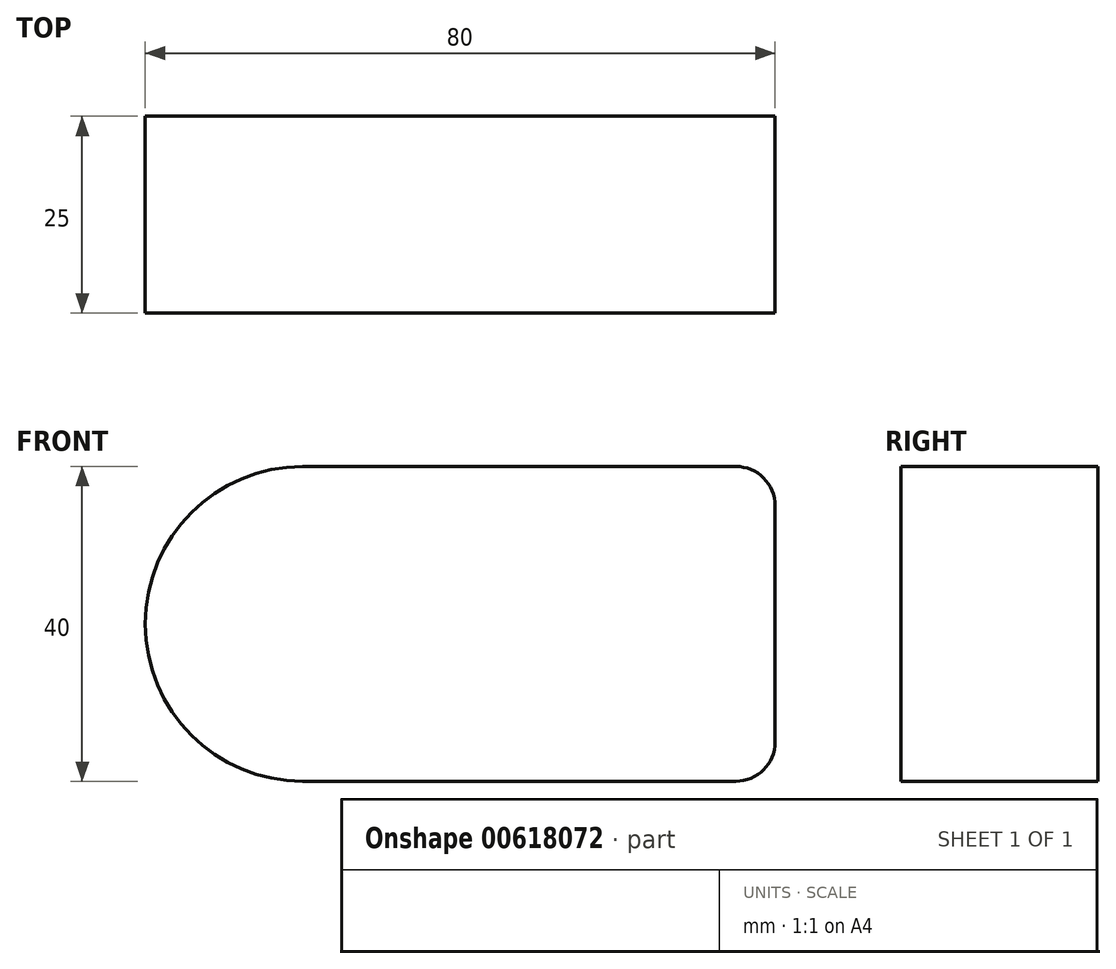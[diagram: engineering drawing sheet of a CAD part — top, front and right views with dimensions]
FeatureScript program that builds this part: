
annotation { "Feature Type Name" : "Feature", "Feature Type Description" : "" }
export const myFeature = defineFeature(function(context is Context, id is Id, definition is map)
    precondition{}
    {
        {
            var Q0;
            Q0=qCreatedBy(makeId("Front.planeOp"),FACE);
            var sketch = newSketch(context, id + "F0", { "sketchPlane" : qUnion([Q0])});
            skLineSegment(sketch, "E0.bottom", {"start": v(0, 0) * mm, "end": v(80, 0) * mm});
            skLineSegment(sketch, "E0.top", {"start": v(0, 40) * mm, "end": v(80, 40) * mm});
            skLineSegment(sketch, "E0.left", {"start": v(0, 0) * mm, "end": v(0, 40) * mm});
            skLineSegment(sketch, "E0.right", {"start": v(80, 0) * mm, "end": v(80, 40) * mm});
            skSolve(sketch);
        }
        {
            var Q0;
            Q0 = qSketchRegion(id + "F0", true);
            extrude(context, id + "F1", {"entities" : qUnion([Q0]), "depth" : 25 * mm, "offsetDistance" : 25 * mm});
        }
        {
            var Q0;
            Q0=makeQuery(id+"F1.opExtrude","SWEPT_EDGE",EDGE,{"disambiguationData":[OSD([sQuery(id+"F0.wireOp",EDGE,"E0.top"),sQuery(id+"F0.wireOp",EDGE,"E0.left")])]});
            fillet(context, id + "F2", {"entities" : qUnion([Q0]), "radius" : 20 * mm, "tangentPropagation" : true, "allowEdgeOverflow" : false});
        }
        {
            var Q0;
            Q0=makeQuery(id+"F1.opExtrude","SWEPT_EDGE",EDGE,{"disambiguationData":[OSD([sQuery(id+"F0.wireOp",EDGE,"E0.bottom"),sQuery(id+"F0.wireOp",EDGE,"E0.left")])]});
            fillet(context, id + "F3", {"entities" : qUnion([Q0]), "radius" : 20 * mm, "tangentPropagation" : true, "allowEdgeOverflow" : false});
        }
        {
            var Q0;
            Q0=makeQuery(id+"F1.opExtrude","SWEPT_EDGE",EDGE,{"disambiguationData":[OSD([sQuery(id+"F0.wireOp",EDGE,"E0.top"),sQuery(id+"F0.wireOp",EDGE,"E0.right")])]});
            var Q1;
            Q1=makeQuery(id+"F1.opExtrude","SWEPT_EDGE",EDGE,{"disambiguationData":[OSD([sQuery(id+"F0.wireOp",EDGE,"E0.bottom"),sQuery(id+"F0.wireOp",EDGE,"E0.right")])]});
            fillet(context, id + "F4", {"entities" : qUnion([Q0, Q1]), "radius" : 5 * mm, "tangentPropagation" : true, "allowEdgeOverflow" : false});
        }
    });
